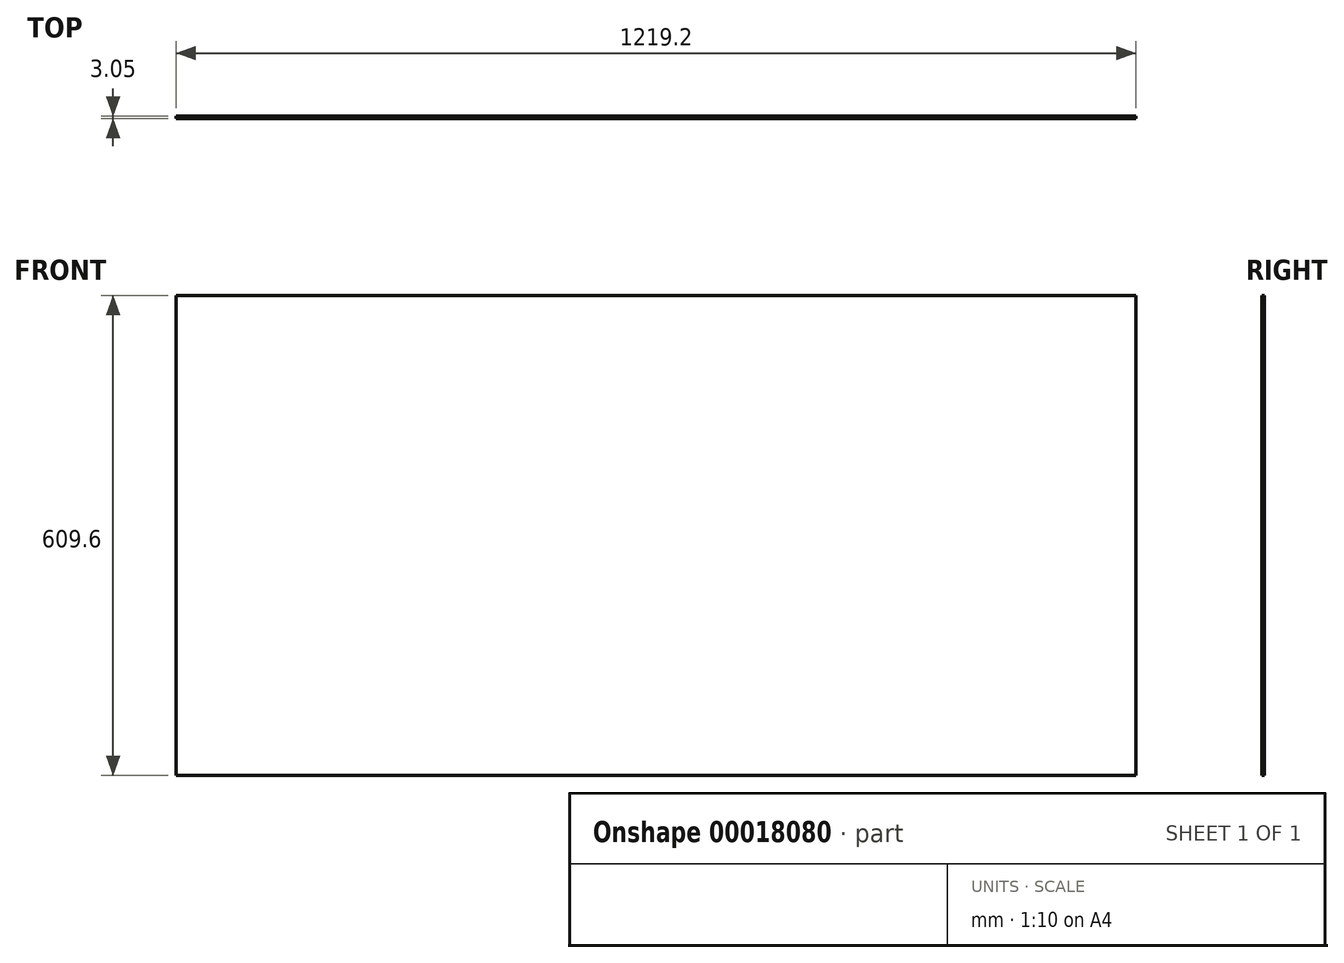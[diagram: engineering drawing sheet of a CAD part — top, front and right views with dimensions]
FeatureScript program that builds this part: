
annotation { "Feature Type Name" : "Feature", "Feature Type Description" : "" }
export const myFeature = defineFeature(function(context is Context, id is Id, definition is map)
    precondition{}
    {
        {
            var Q0;
            Q0=qCreatedBy(makeId("Front.planeOp"),FACE);
            var sketch = newSketch(context, id + "F0", { "sketchPlane" : qUnion([Q0])});
            skLineSegment(sketch, "E0.bottom", {"start": v(-607.94, -320.03) * mm, "end": v(611.26, -320.03) * mm});
            skLineSegment(sketch, "E0.top", {"start": v(-607.94, 289.57) * mm, "end": v(611.26, 289.57) * mm});
            skLineSegment(sketch, "E0.left", {"start": v(-607.94, -320.03) * mm, "end": v(-607.94, 289.57) * mm});
            skLineSegment(sketch, "E0.right", {"start": v(611.26, -320.03) * mm, "end": v(611.26, 289.57) * mm});
            skSolve(sketch);
        }
        {
            var Q0;
            Q0 = qSketchRegion(id + "F0", true);
            extrude(context, id + "F1", {"entities" : qUnion([Q0]), "depth" : 3.05 * mm});
        }
    });
